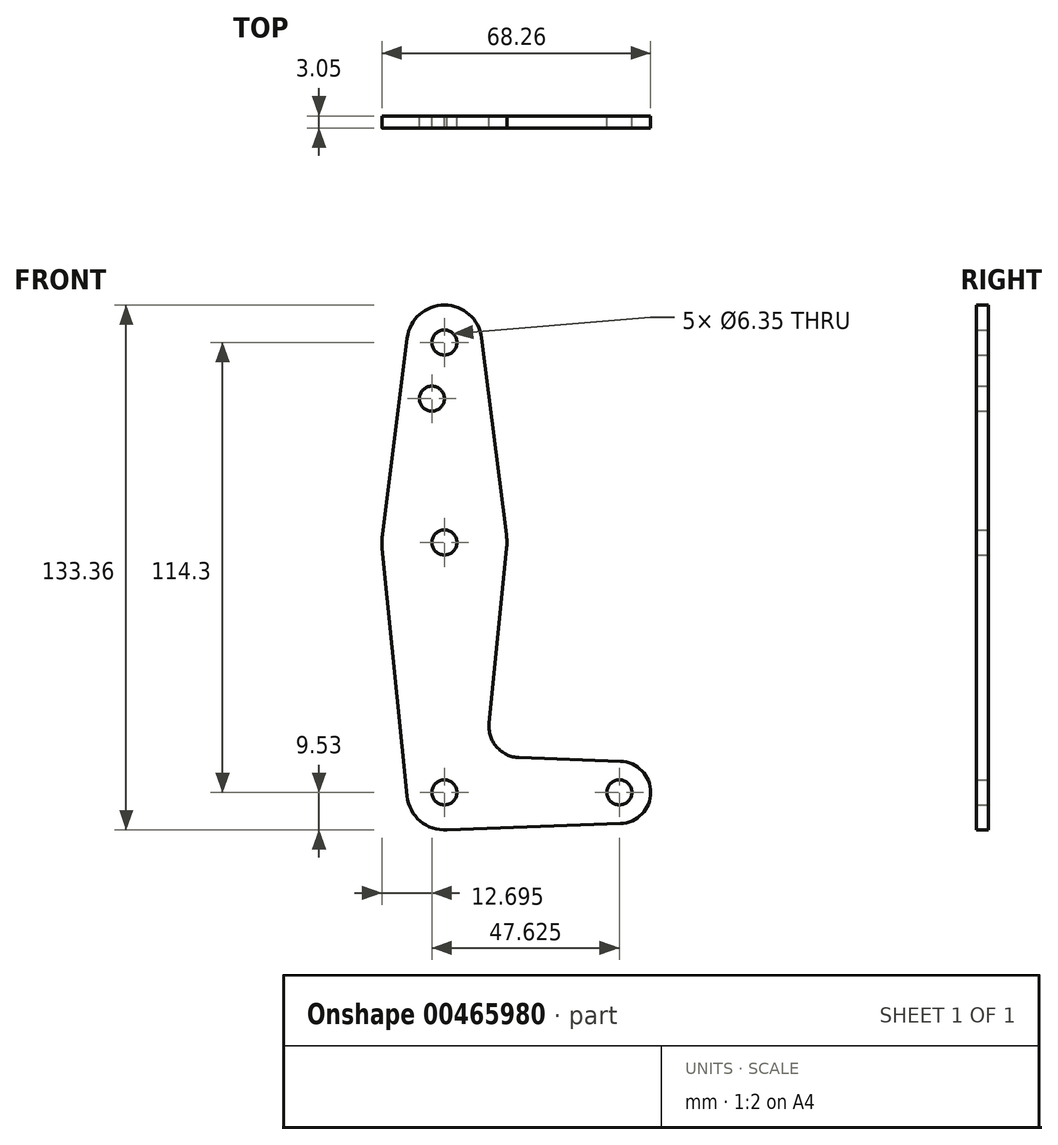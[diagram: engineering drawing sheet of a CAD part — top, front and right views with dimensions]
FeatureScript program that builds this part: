
annotation { "Feature Type Name" : "Feature", "Feature Type Description" : "" }
export const myFeature = defineFeature(function(context is Context, id is Id, definition is map)
    precondition{}
    {
        {
            var Q0;
            Q0=qCreatedBy(makeId("Front.planeOp"),FACE);
            var sketch = newSketch(context, id + "F0", { "sketchPlane" : qUnion([Q0])});
            skLineSegment(sketch, "E0", {"start": v(0, 0) * mm, "end": v(0, 114.3) * mm, "construction": true});
            skLineSegment(sketch, "E1", {"start": v(0, 0) * mm, "end": v(44.45, 0) * mm, "construction": true});
            skCircle(sketch, "E2", {"center": v(0, 114.3) * mm, "radius": 9.53 * mm});
            skCircle(sketch, "E3", {"center": v(0, 0) * mm, "radius": 9.53 * mm});
            skCircle(sketch, "E4", {"center": v(0, 63.5) * mm, "radius": 15.88 * mm});
            skCircle(sketch, "E5", {"center": v(44.45, 0) * mm, "radius": 7.94 * mm});
            skLineSegment(sketch, "E6", {"start": v(-9.45, 115.5) * mm, "end": v(-15.75, 65.48) * mm});
            skLineSegment(sketch, "E7", {"start": v(9.45, 115.5) * mm, "end": v(15.75, 65.48) * mm});
            skLineSegment(sketch, "E8", {"start": v(-15.8, 61.91) * mm, "end": v(-9.48, -0.95) * mm});
            skLineSegment(sketch, "E9", {"start": v(15.8, 61.91) * mm, "end": v(11.34, 17.59) * mm});
            skLineSegment(sketch, "E10", {"start": v(18.97, 8.85) * mm, "end": v(44.73, 7.93) * mm});
            skLineSegment(sketch, "E11", {"start": v(0, -9.53) * mm, "end": v(44.73, -7.93) * mm});
            skCircle(sketch, "E12", {"center": v(0, 114.3) * mm, "radius": 3.18 * mm});
            skCircle(sketch, "E13", {"center": v(0, 63.5) * mm, "radius": 3.18 * mm});
            skCircle(sketch, "E14", {"center": v(0, 0) * mm, "radius": 3.18 * mm});
            skCircle(sketch, "E15", {"center": v(44.45, 0) * mm, "radius": 3.18 * mm});
            skCircle(sketch, "E16", {"center": v(-3.18, 100.03) * mm, "radius": 3.18 * mm});
            skPoint(sketch, "E17.newPointA", {"position": v(9.48, -0.95) * mm});
            skArc(sketch, "E17.filletArc", {"start": v(11.34, 17.59) * mm, "mid": v(13.26, 11.57) * mm, "end": v(18.97, 8.85) * mm});
            skSolve(sketch);
        }
        {
            var Q0;
            Q0 = qSketchRegion(id + "F0", true);
            extrude(context, id + "F1", {"entities" : qUnion([Q0]), "depth" : 3.05 * mm});
        }
    });
